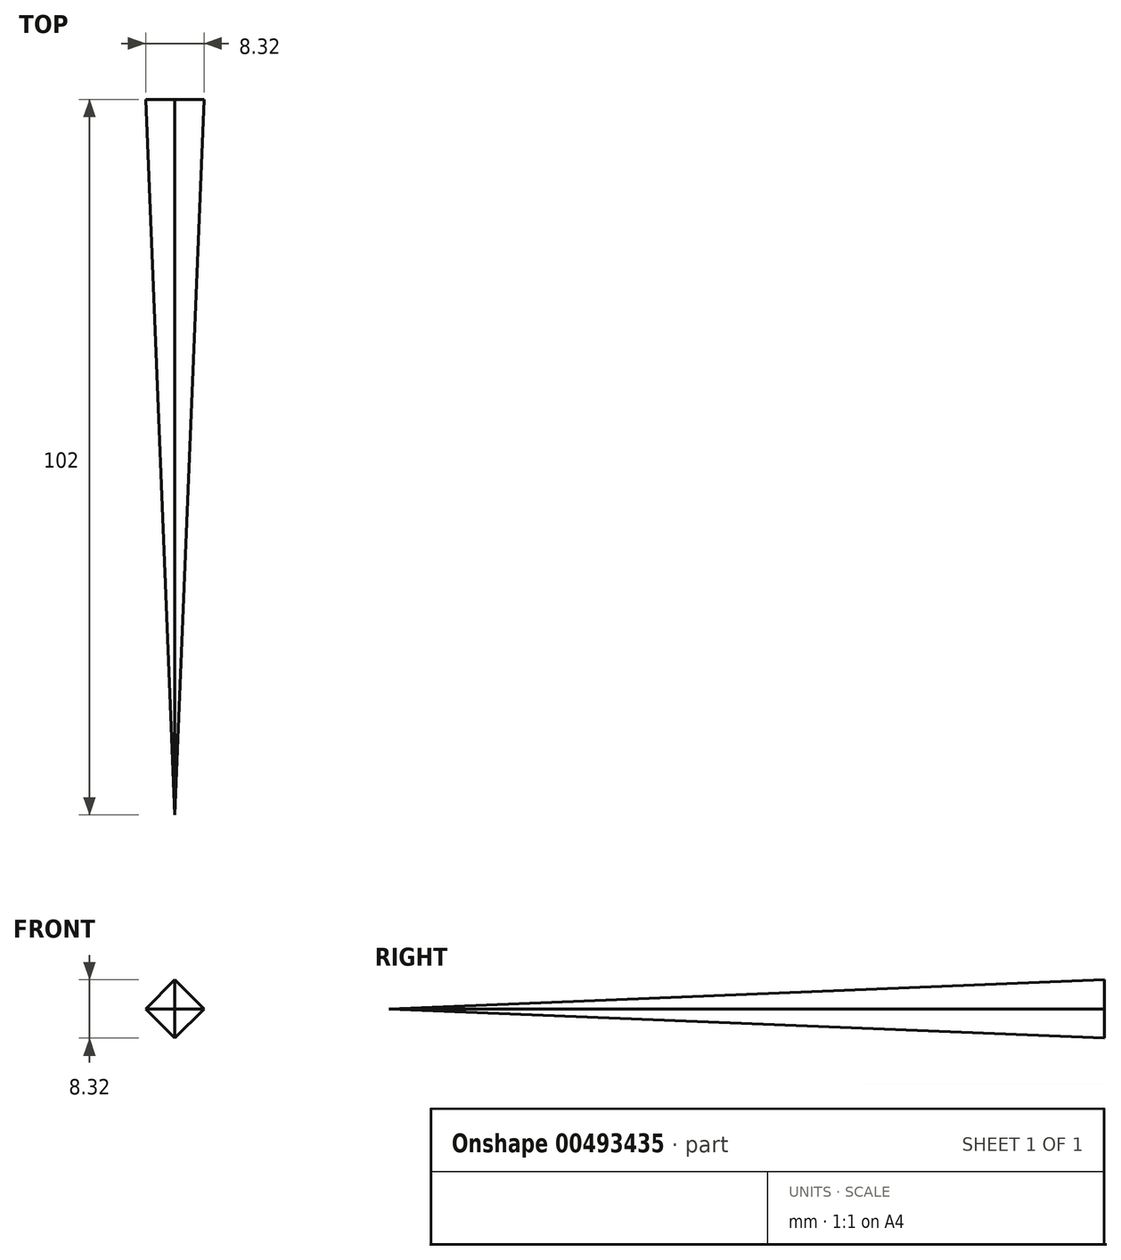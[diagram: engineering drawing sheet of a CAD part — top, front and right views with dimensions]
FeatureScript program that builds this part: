
annotation { "Feature Type Name" : "Feature", "Feature Type Description" : "" }
export const myFeature = defineFeature(function(context is Context, id is Id, definition is map)
    precondition{}
    {
        {
            var Q0;
            Q0=qCreatedBy(makeId("Front.planeOp"),FACE);
            var sketch = newSketch(context, id + "F0", { "sketchPlane" : qUnion([Q0])});
            skCircle(sketch, "E0.cCircle", {"center": v(0, 0) * mm, "radius": 4.16 * mm, "construction": true});
            skLineSegment(sketch, "E0.0", {"start": v(0, 4.16) * mm, "end": v(4.16, 0) * mm});
            skLineSegment(sketch, "E0.1", {"start": v(4.16, 0) * mm, "end": v(0, -4.16) * mm});
            skLineSegment(sketch, "E0.2", {"start": v(0, -4.16) * mm, "end": v(-4.16, 0) * mm});
            skLineSegment(sketch, "E0.3", {"start": v(-4.16, 0) * mm, "end": v(0, 4.16) * mm});
            skSolve(sketch);
        }
        {
            var Q0;
            Q0=qCreatedBy(makeId("Front.planeOp"),FACE);
            cPlane(context, id + "F1", {"entities" : qUnion([Q0]), "cplaneType" : CPlaneType.OFFSET, "offset" : 102 * mm, "width" : 150 * mm, "height" : 150 * mm});
        }
        {
            var Q0;
            Q0=qCreatedBy(id+"F1.planeOp",FACE);
            var sketch = newSketch(context, id + "F2", { "sketchPlane" : qUnion([Q0])});
            skCircle(sketch, "E1", {"center": v(0, 0) * mm, "radius": 1.18 * mm});
            skSolve(sketch);
        }
        {
            var Q0;
            Q0=sQuery(id+"F2.wireOp",VERTEX,"E1.center");
            var Q1;
            Q1=makeQuery(id+"F0.imprint","IMPRINT",FACE,{"disambiguationData":[TD([[makeQuery(id+"F0.imprint","IMPRINT",EDGE,{"derivedFrom":sQuery(id+"F0.wireOp",EDGE,"E0.0")}),-1.0]])]});
            loft(context, id + "F3", {"sheetProfilesArray" : [{ "sheetProfileEntities" : qUnion([Q0]) }, { "sheetProfileEntities" : qUnion([Q1]) }]});
        }
    });
